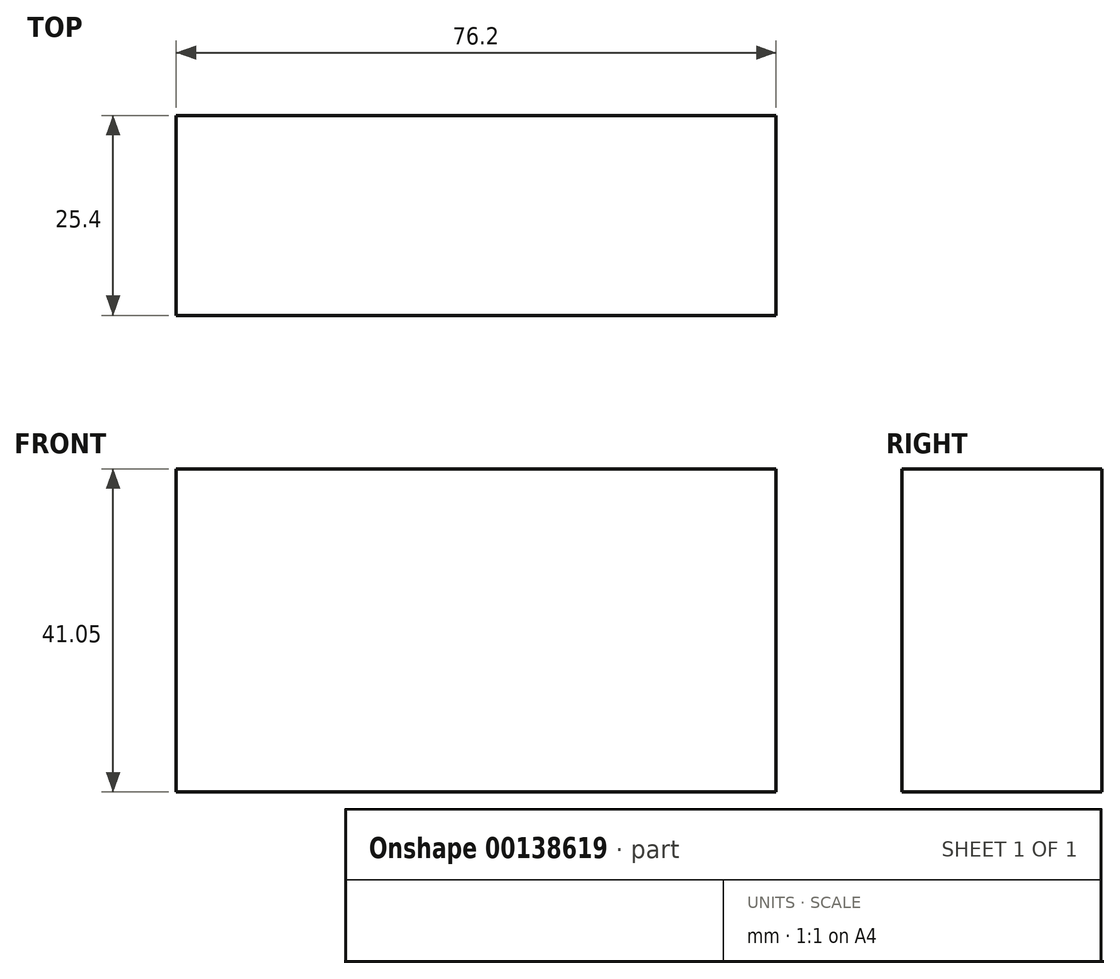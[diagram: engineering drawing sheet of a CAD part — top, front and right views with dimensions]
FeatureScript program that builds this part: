
annotation { "Feature Type Name" : "Feature", "Feature Type Description" : "" }
export const myFeature = defineFeature(function(context is Context, id is Id, definition is map)
    precondition{}
    {
        {
            var Q0;
            Q0=qCreatedBy(makeId("Front.planeOp"),FACE);
            var sketch = newSketch(context, id + "F0", { "sketchPlane" : qUnion([Q0])});
            skLineSegment(sketch, "E0.bottom", {"start": v(0, 0) * mm, "end": v(-76.2, 0) * mm});
            skLineSegment(sketch, "E0.top", {"start": v(0, 41.05) * mm, "end": v(-76.2, 41.05) * mm});
            skLineSegment(sketch, "E0.left", {"start": v(0, 0) * mm, "end": v(0, 41.05) * mm});
            skLineSegment(sketch, "E0.right", {"start": v(-76.2, 0) * mm, "end": v(-76.2, 41.05) * mm});
            skSolve(sketch);
        }
        {
            var Q0;
            Q0=makeQuery(id+"F0.imprint","IMPRINT",FACE,{"disambiguationData":[TD([[makeQuery(id+"F0.imprint","IMPRINT",EDGE,{"derivedFrom":sQuery(id+"F0.wireOp",EDGE,"E0.bottom")}),-1.0]])]});
            extrude(context, id + "F1", {"entities" : qUnion([Q0]), "depth" : 25.4 * mm});
        }
    });
